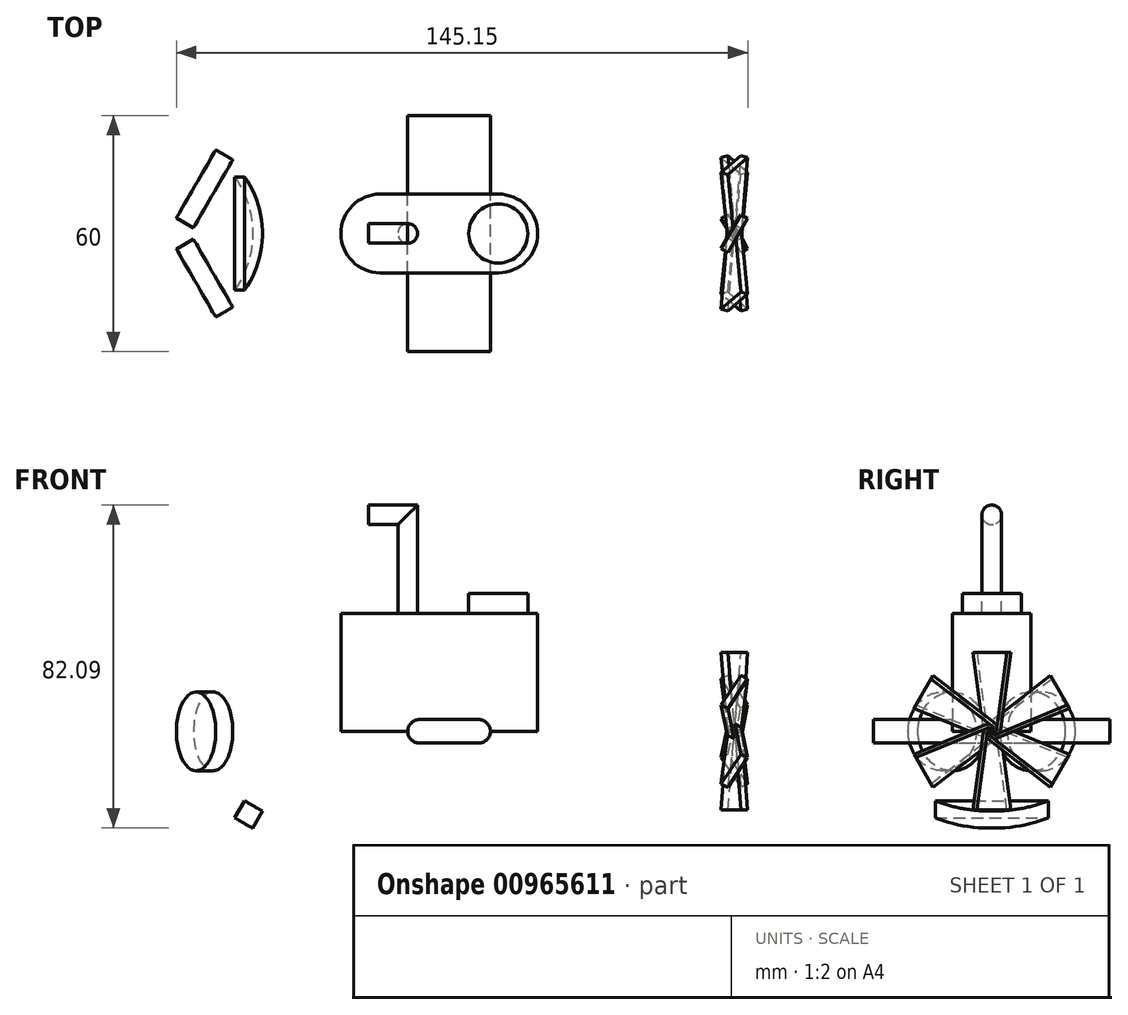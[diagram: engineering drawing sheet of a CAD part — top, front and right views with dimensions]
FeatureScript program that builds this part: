
annotation { "Feature Type Name" : "Feature", "Feature Type Description" : "" }
export const myFeature = defineFeature(function(context is Context, id is Id, definition is map)
    precondition{}
    {
        {
            var Q0;
            Q0=qCreatedBy(makeId("Front.planeOp"),FACE);
            var sketch = newSketch(context, id + "F0", { "sketchPlane" : qUnion([Q0])});
            skLineSegment(sketch, "E0", {"start": v(0, 0) * mm, "end": v(150, 0) * mm});
            skArc(sketch, "E1", {"start": v(28.26, 24.79) * mm, "mid": v(8.52, 18.8) * mm, "end": v(0, 0) * mm});
            skArc(sketch, "E2", {"start": v(150, 0) * mm, "mid": v(147.52, 6.6) * mm, "end": v(141.3, 9.91) * mm});
            skLineSegment(sketch, "E3", {"start": v(28.26, 24.79) * mm, "end": v(141.3, 9.91) * mm});
            skSolve(sketch);
        }
        {
            var Q0;
            Q0=sQuery(id+"F0.wireOp",EDGE,"E3");
            var Q1;
            Q1=sQuery(id+"F0.wireOp",EDGE,"E1");
            var Q2;
            Q2=sQuery(id+"F0.wireOp",EDGE,"E2");
            var Q3;
            Q3=sQuery(id+"F0.wireOp",EDGE,"E0");
            revolve(context, id + "F1", {"bodyType" : ToolBodyType.SURFACE, "surfaceOperationType" : NewSurfaceOperationType.NEW, "surfaceEntities" : qUnion([Q0, Q1, Q2]), "axis" : qUnion([Q3]), "revolveType" : RevolveType.FULL});
        }
        {
            var Q0;
            Q0=qCreatedBy(makeId("Top.planeOp"),FACE);
            var sketch = newSketch(context, id + "F2", { "sketchPlane" : qUnion([Q0])});
            skLineSegment(sketch, "E4.bottom", {"start": v(50, 10) * mm, "end": v(80, 10) * mm});
            skLineSegment(sketch, "E4.top", {"start": v(50, -10) * mm, "end": v(80, -10) * mm});
            skPoint(sketch, "E4.middle", {"position": v(65, 0) * mm});
            skArc(sketch, "E5", {"start": v(50, 10) * mm, "mid": v(40, 0) * mm, "end": v(50, -10) * mm});
            skArc(sketch, "E6", {"start": v(80, -10) * mm, "mid": v(90, 0) * mm, "end": v(80, 10) * mm});
            skSolve(sketch);
        }
        {
            var Q0;
            Q0 = qSketchRegion(id + "F2", true);
            extrude(context, id + "F3", {"entities" : qUnion([Q0]), "depth" : 30 * mm, "offsetDistance" : 25 * mm});
        }
        {
            var Q0;
            Q0=makeQuery(id+"F3.opExtrude","CAP_FACE",FACE,{"disambiguationData":[OSD([sQuery(id+"F2.wireOp",EDGE,"E4.bottom"),sQuery(id+"F2.wireOp",EDGE,"E4.top"),sQuery(id+"F2.wireOp",EDGE,"E5"),sQuery(id+"F2.wireOp",EDGE,"E6")])],"isStart":false});
            var sketch = newSketch(context, id + "F4", { "sketchPlane" : qUnion([Q0])});
            skCircle(sketch, "E7", {"center": v(80, 0) * mm, "radius": 7.5 * mm});
            skSolve(sketch);
        }
        {
            var Q0;
            Q0=makeQuery(id+"F4.imprint","IMPRINT",FACE,{"disambiguationData":[TD([[makeQuery(id+"F4.imprint","IMPRINT",EDGE,{"derivedFrom":sQuery(id+"F4.wireOp",EDGE,"E7")}),1.0]])]});
            extrude(context, id + "F5", {"entities" : qUnion([Q0]), "operationType" : NewBodyOperationType.ADD, "depth" : 5 * mm, "offsetDistance" : 25 * mm});
        }
        {
            var Q0;
            Q0=qCreatedBy(makeId("Front.planeOp"),FACE);
            var sketch = newSketch(context, id + "F6", { "sketchPlane" : qUnion([Q0])});
            skLineSegment(sketch, "E8.0", {"start": v(50, 30) * mm, "end": v(80, 30) * mm, "construction": true});
            skLineSegment(sketch, "E9", {"start": v(57, 30) * mm, "end": v(57, 55) * mm});
            skLineSegment(sketch, "E10", {"start": v(57, 55) * mm, "end": v(47, 55) * mm});
            skSolve(sketch);
        }
        {
            var Q0;
            Q0=makeQuery(id+"F3.opExtrude","CAP_FACE",FACE,{"disambiguationData":[OSD([sQuery(id+"F2.wireOp",EDGE,"E4.bottom"),sQuery(id+"F2.wireOp",EDGE,"E4.top"),sQuery(id+"F2.wireOp",EDGE,"E5"),sQuery(id+"F2.wireOp",EDGE,"E6")])],"isStart":false});
            var sketch = newSketch(context, id + "F7", { "sketchPlane" : qUnion([Q0])});
            skPoint(sketch, "E11.0", {"position": v(57, 0) * mm});
            skCircle(sketch, "E12", {"center": v(57, 0) * mm, "radius": 2.5 * mm});
            skSolve(sketch);
        }
        {
            var Q0;
            Q0=makeQuery(id+"F7.imprint","IMPRINT",FACE,{"disambiguationData":[TD([[makeQuery(id+"F7.imprint","IMPRINT",EDGE,{"derivedFrom":sQuery(id+"F7.wireOp",EDGE,"E12")}),1.0]])]});
            var Q1;
            Q1=sQuery(id+"F6.wireOp",EDGE,"E9");
            var Q2;
            Q2=sQuery(id+"F6.wireOp",EDGE,"E10");
            sweep(context, id + "F8", {"operationType" : NewBodyOperationType.ADD, "profiles" : qUnion([Q0]), "path" : qUnion([Q1, Q2])});
        }
        {
            var Q0;
            Q0=qCreatedBy(makeId("Front.planeOp"),FACE);
            var sketch = newSketch(context, id + "F9", { "sketchPlane" : qUnion([Q0])});
            skLineSegment(sketch, "E13.bottom", {"start": v(130, 20) * mm, "end": v(150, 20) * mm});
            skLineSegment(sketch, "E13.top", {"start": v(130, 22) * mm, "end": v(150, 22) * mm});
            skLineSegment(sketch, "E13.left", {"start": v(130, 20) * mm, "end": v(130, 22) * mm});
            skLineSegment(sketch, "E13.right", {"start": v(150, 20) * mm, "end": v(150, 22) * mm});
            skLineSegment(sketch, "E14", {"start": v(0, 0) * mm, "end": v(215.45, 0) * mm, "construction": true});
            skSolve(sketch);
        }
        {
            var Q0;
            Q0=sQuery(id+"F9.wireOp",EDGE,"E13.top");
            var Q1;
            Q1=sQuery(id+"F9.wireOp",EDGE,"E13.right");
            var Q2;
            Q2=sQuery(id+"F9.wireOp",EDGE,"E13.bottom");
            var Q3;
            Q3=sQuery(id+"F9.wireOp",EDGE,"E13.left");
            var Q4;
            Q4=sQuery(id+"F9.wireOp",EDGE,"E14");
            revolve(context, id + "F10", {"bodyType" : ToolBodyType.SURFACE, "surfaceOperationType" : NewSurfaceOperationType.NEW, "surfaceEntities" : qUnion([Q0, Q1, Q2, Q3]), "axis" : qUnion([Q4]), "revolveType" : RevolveType.FULL});
        }
        {
            var Q0;
            Q0=makeQuery(id+"F10.opRevolve","SWEPT_FACE",FACE,{"disambiguationData":[OSD([sQuery(id+"F9.wireOp",EDGE,"E13.right")])]});
            cPlane(context, id + "F11", {"entities" : qUnion([Q0]), "cplaneType" : CPlaneType.OFFSET, "offset" : 10 * mm, "width" : 150 * mm, "height" : 150 * mm});
        }
        {
            var Q0;
            Q0=qCreatedBy(id+"F11.planeOp",FACE);
            var sketch = newSketch(context, id + "F12", { "sketchPlane" : qUnion([Q0])});
            skLineSegment(sketch, "E15", {"start": v(0, 0) * mm, "end": v(0, -55.18) * mm});
            skSolve(sketch);
        }
        {
            var Q0;
            Q0=sQuery(id+"F12.wireOp",EDGE,"E15");
            var Q1;
            Q1=qCreatedBy(id+"F11.planeOp",FACE);
            cPlane(context, id + "F13", {"entities" : qUnion([Q0, Q1]), "cplaneType" : CPlaneType.LINE_ANGLE, "offset" : 25 * mm, "angle" : 30 * degree, "width" : 150 * mm, "height" : 150 * mm});
        }
        {
            var Q0;
            Q0=qCreatedBy(id+"F13.planeOp",FACE);
            var sketch = newSketch(context, id + "F14", { "sketchPlane" : qUnion([Q0])});
            skEllipse(sketch, "E16.0", {"center": v(75, 0) * mm, "majorRadius": 20 * mm, "minorRadius": 17.32 * mm, "majorAxis": v(0, -1), "construction": true});
            skLineSegment(sketch, "E17", {"start": v(71.9, 0) * mm, "end": v(75, 20) * mm});
            skEllipse(sketch, "E18.0", {"center": v(65, 0) * mm, "majorRadius": 20 * mm, "minorRadius": 17.32 * mm, "majorAxis": v(0, -1), "construction": true});
            skLineSegment(sketch, "E19", {"start": v(75, 20) * mm, "end": v(65, 20) * mm});
            skLineSegment(sketch, "E20", {"start": v(65, 20) * mm, "end": v(68.1, 0) * mm});
            skLineSegment(sketch, "E21", {"start": v(68.1, 0) * mm, "end": v(71.9, 0) * mm});
            skLineSegment(sketch, "E22", {"start": v(70, 20) * mm, "end": v(70, 0) * mm});
            skLineSegment(sketch, "E23", {"start": v(0, 0) * mm, "end": v(110.48, 0) * mm, "construction": true});
            skPoint(sketch, "E23.endSnap0", {"position": v(82.32, 0) * mm});
            skSolve(sketch);
        }
        {
            var Q0;
            {var subQ0=sQuery(id+"F14.wireOp",EDGE,"E20");Q0=makeQuery(id+"F14.imprint","IMPRINT",FACE,{"disambiguationData":[TD([[makeQuery(id+"F14.imprint","IMPRINT",EDGE,{"derivedFrom":subQ0}),1.0]])]});}
            var Q1;
            {var subQ0=sQuery(id+"F14.wireOp",EDGE,"E17");Q1=makeQuery(id+"F14.imprint","IMPRINT",FACE,{"disambiguationData":[TD([[makeQuery(id+"F14.imprint","IMPRINT",EDGE,{"derivedFrom":subQ0}),1.0]])]});}
            var Q2;
            Q2=sQuery(id+"F14.wireOp",EDGE,"E20");
            var Q3;
            Q3=sQuery(id+"F14.wireOp",EDGE,"E19");
            var Q4;
            Q4=sQuery(id+"F14.wireOp",EDGE,"E17");
            var Q5;
            Q5=sQuery(id+"F14.wireOp",EDGE,"E21");
            extrude(context, id + "F15", {"entities" : qUnion([Q0, Q1]), "surfaceEntities" : qUnion([Q2, Q3, Q4, Q5]), "depth" : 1 * mm, "offsetDistance" : 25 * mm, "hasSecondDirection" : true, "secondDirectionOppositeDirection" : true, "secondDirectionDepth" : 1 * mm});
        }
        {
            var Q0;
            Q0=makeQuery(id+"F15.opExtrude","SWEPT_BODY",BODY,{"disambiguationData":[OSD([sQuery(id+"F14.wireOp",EDGE,"E17"),sQuery(id+"F14.wireOp",EDGE,"E19"),sQuery(id+"F14.wireOp",EDGE,"E20"),sQuery(id+"F14.wireOp",EDGE,"E21")])]});
            var Q1;
            Q1=makeQuery(id+"F1.opRevolve","SWEPT_FACE",FACE,{"disambiguationData":[OSD([sQuery(id+"F0.wireOp",EDGE,"E3")])]});
            circularPattern(context, id + "F16", {"entities" : qUnion([Q0]), "axis" : qUnion([Q1]), "angle" : 360 * degree, "instanceCount" : 6, "equalSpace" : true});
        }
        {
            var Q0;
            Q0=qCreatedBy(makeId("Front.planeOp"),FACE);
            var sketch = newSketch(context, id + "F17", { "sketchPlane" : qUnion([Q0])});
            skLineSegment(sketch, "E24.bottom", {"start": v(60, -3) * mm, "end": v(75, -3) * mm});
            skLineSegment(sketch, "E24.top", {"start": v(60, 3) * mm, "end": v(75, 3) * mm});
            skLineSegment(sketch, "E25", {"start": v(0, 0) * mm, "end": v(150.4, 0) * mm, "construction": true});
            skArc(sketch, "E26", {"start": v(60, 3) * mm, "mid": v(57, 0) * mm, "end": v(60, -3) * mm});
            skArc(sketch, "E27", {"start": v(75, -3) * mm, "mid": v(78, 0) * mm, "end": v(75, 3) * mm});
            skSolve(sketch);
        }
        {
            var Q0;
            Q0 = qSketchRegion(id + "F17", true);
            extrude(context, id + "F18", {"entities" : qUnion([Q0]), "operationType" : NewBodyOperationType.ADD, "depth" : 30 * mm, "offsetDistance" : 25 * mm, "hasSecondDirection" : true, "secondDirectionOppositeDirection" : true, "secondDirectionDepth" : 30 * mm});
        }
        {
            var Q0;
            Q0=qCreatedBy(makeId("Right.planeOp"),FACE);
            var sketch = newSketch(context, id + "F19", { "sketchPlane" : qUnion([Q0])});
            skLineSegment(sketch, "E28", {"start": v(0, 0) * mm, "end": v(0, 65.11) * mm});
            skSolve(sketch);
        }
        {
            var Q0;
            Q0=qCreatedBy(makeId("Right.planeOp"),FACE);
            var Q1;
            Q1 = qBodyType(qCreatedBy(id + "F19" ,EDGE), BodyType.WIRE);
            cPlane(context, id + "F20", {"entities" : qUnion([Q0, Q1]), "cplaneType" : CPlaneType.LINE_ANGLE, "offset" : 25 * mm, "angle" : 30 * degree, "width" : 150 * mm, "height" : 150 * mm});
        }
        {
            var Q0;
            Q0=qCreatedBy(id+"F20.planeOp",FACE);
            cPlane(context, id + "F21", {"entities" : qUnion([Q0]), "cplaneType" : CPlaneType.OFFSET, "offset" : 3.5 * mm, "width" : 150 * mm, "height" : 150 * mm});
        }
        {
            var Q0;
            Q0=qCreatedBy(id+"F21.planeOp",FACE);
            var sketch = newSketch(context, id + "F22", { "sketchPlane" : qUnion([Q0])});
            skLineSegment(sketch, "E29", {"start": v(0, 0) * mm, "end": v(35.6, 0) * mm, "construction": true});
            skCircle(sketch, "E30", {"center": v(12.5, 0) * mm, "radius": 10 * mm});
            skSolve(sketch);
        }
        {
            var Q0;
            Q0 = qSketchRegion(id + "F22", true);
            extrude(context, id + "F23", {"entities" : qUnion([Q0]), "operationType" : NewBodyOperationType.ADD, "oppositeDirection" : true, "depth" : 5 * mm, "offsetDistance" : 25 * mm});
        }
        {
            var Q0;
            Q0=makeQuery(id+"F23.opExtrude","SWEPT_BODY",BODY,{"disambiguationData":[OSD([sQuery(id+"F22.wireOp",EDGE,"E30")])]});
            var Q1;
            Q1=qCreatedBy(makeId("Front.planeOp"),FACE);
            mirror(context, id + "F24", {"entities" : qUnion([Q0]), "mirrorPlane" : qUnion([Q1])});
        }
        {
            var Q0;
            Q0=qCreatedBy(makeId("Right.planeOp"),FACE);
            var sketch = newSketch(context, id + "F25", { "sketchPlane" : qUnion([Q0])});
            skLineSegment(sketch, "E31", {"start": v(0, 0) * mm, "end": v(-72.49, 0) * mm});
            skSolve(sketch);
        }
        {
            var Q0;
            Q0=qCreatedBy(makeId("Right.planeOp"),FACE);
            var Q1;
            Q1=sQuery(id+"F25.wireOp",EDGE,"E31");
            cPlane(context, id + "F26", {"entities" : qUnion([Q0, Q1]), "cplaneType" : CPlaneType.LINE_ANGLE, "offset" : 25 * mm, "angle" : 60 * degree, "width" : 150 * mm, "height" : 150 * mm});
        }
        {
            var Q0;
            Q0=qCreatedBy(id+"F26.planeOp",FACE);
            cPlane(context, id + "F27", {"entities" : qUnion([Q0]), "cplaneType" : CPlaneType.OFFSET, "offset" : 12.5 * mm, "width" : 150 * mm, "height" : 150 * mm});
        }
        {
            var Q0;
            Q0=qCreatedBy(id+"F27.planeOp",FACE);
            var sketch = newSketch(context, id + "F28", { "sketchPlane" : qUnion([Q0])});
            skLineSegment(sketch, "E32", {"start": v(0.94, 0) * mm, "end": v(39.59, 0) * mm, "construction": true});
            skLineSegment(sketch, "E33", {"start": v(22.27, 14.34) * mm, "end": v(22.27, -14.34) * mm});
            skArc(sketch, "E34", {"start": v(22.27, -14.34) * mm, "mid": v(27.54, 0) * mm, "end": v(22.27, 14.34) * mm});
            skSolve(sketch);
        }
        {
            var Q0;
            Q0=makeQuery(id+"F28.imprint","IMPRINT",FACE,{"disambiguationData":[TD([[makeQuery(id+"F28.imprint","IMPRINT",EDGE,{"derivedFrom":sQuery(id+"F28.wireOp",EDGE,"E33")}),1.0]])]});
            var Q1;
            Q1 = qConstructionFilter(qBodyType(qCreatedBy(id + "F28" ,EDGE), BodyType.WIRE), ConstructionObject.NO);
            extrude(context, id + "F29", {"entities" : qUnion([Q0]), "surfaceEntities" : qUnion([Q1]), "oppositeDirection" : true, "depth" : 5 * mm, "offsetDistance" : 25 * mm});
        }
    });
